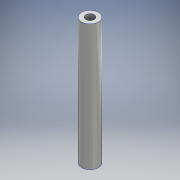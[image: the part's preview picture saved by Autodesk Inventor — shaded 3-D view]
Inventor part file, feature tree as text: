
AUTODESK INVENTOR PART (.ipt)
format: ipt  version: 2020.2 (Build 242310000, 310)  size: 99,328 bytes
history: native  units: mm
features: other x2, extrude x2, sketch x2
ambient origin geometry x8: Origin, YZ Plane, XZ Plane, XY Plane, X Axis, Y Axis, Z Axis, Center Point
bodies: Body1 (feature_tree)
feature tree (6):
  other  "ソリッド1"
  extrude  "押し出し1"  Depth=6.0mm
  other  "作業平面1"
  extrude  "押し出し2"  Depth=3.0mm
  sketch  "スケッチ1"
  sketch  "スケッチ2"
